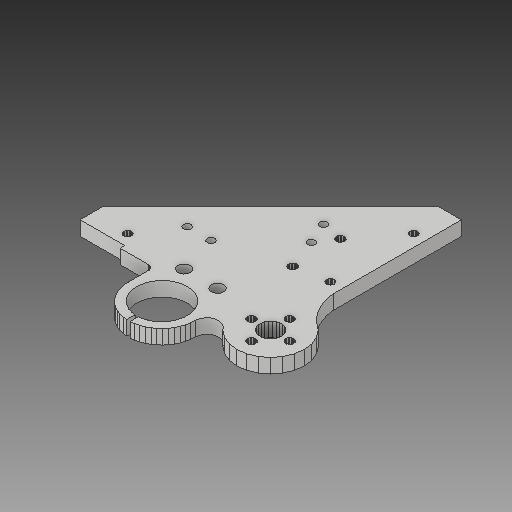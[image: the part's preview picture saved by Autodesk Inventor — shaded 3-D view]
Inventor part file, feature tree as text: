
AUTODESK INVENTOR PART (.ipt)
format: ipt  version: 2018 (Build 220112000, 112)  size: 539,136 bytes
history: native  units: mm
features: extrude x1, hole x1, sketch x1
ambient origin geometry x8: Origin, YZ Plane, XZ Plane, XY Plane, X Axis, Y Axis, Z Axis, Center Point
bodies: Solid1 (feature_tree)
feature tree (3):
  extrude  "Extrusion1"  [1 undecoded]
  hole  "Hole1"  [1 undecoded]
  sketch  "Sketch2"  dims[d0=6.0mm d1=0.0mm d2=21.2mm d3=6.0mm d4=4.0mm d5=2.0mm d6=90.0deg d7=8.0mm d8=20.594885mm]
note: 2 required parameter values undecoded (feature->parameter linkage not recoverable at this tier; creation-order binding heuristic only, values carry confidence <= 0.55)
